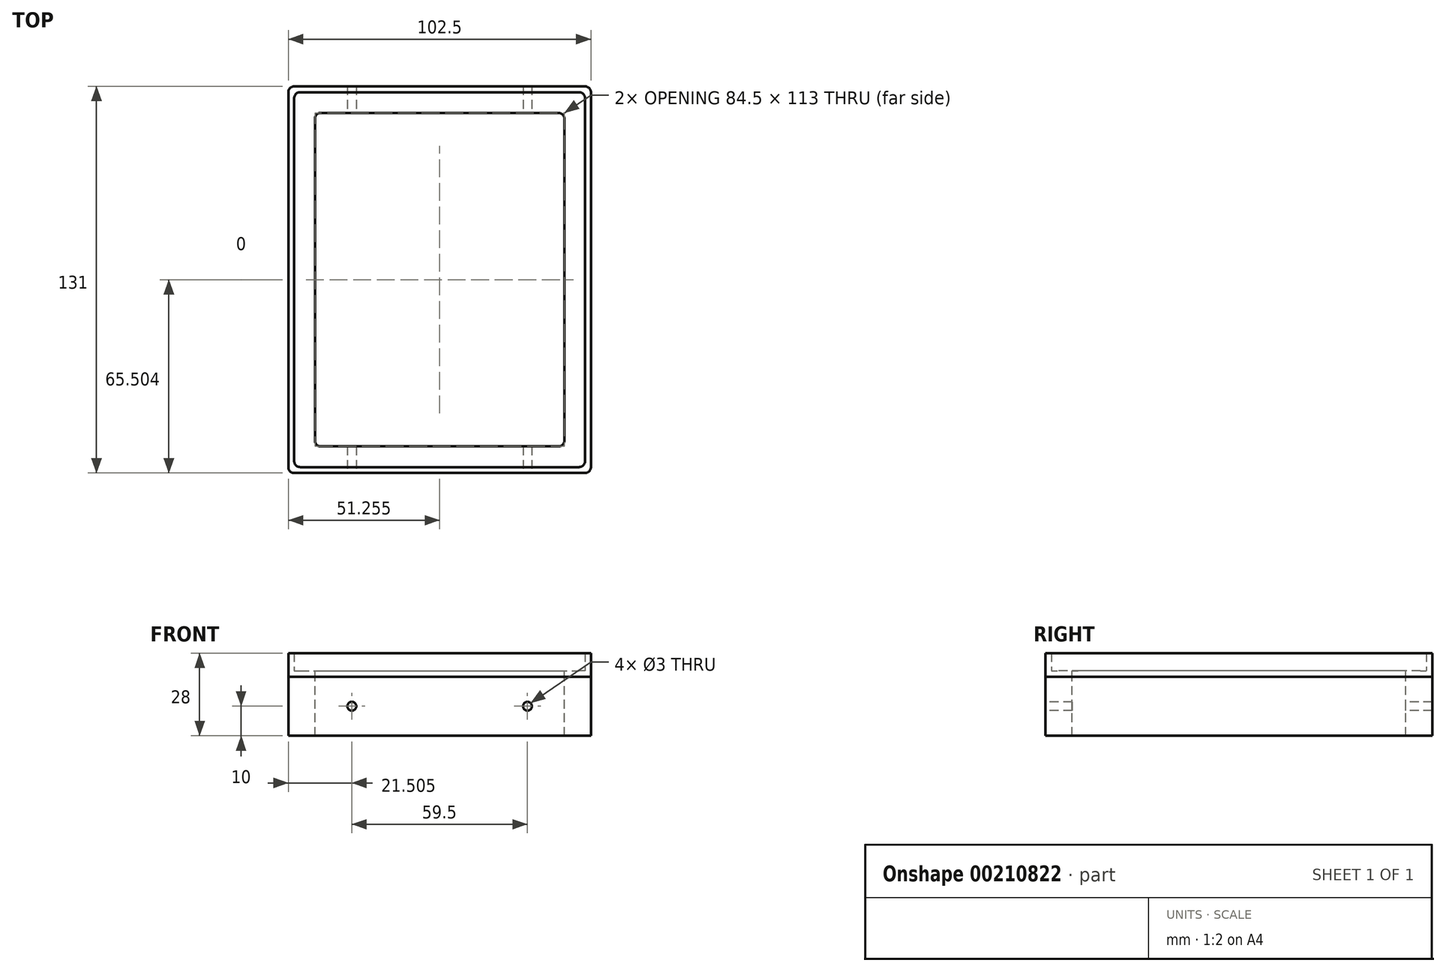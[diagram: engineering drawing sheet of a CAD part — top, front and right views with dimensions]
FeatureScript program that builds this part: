
annotation { "Feature Type Name" : "Feature", "Feature Type Description" : "" }
export const myFeature = defineFeature(function(context is Context, id is Id, definition is map)
    precondition{}
    {
        {
            var Q0;
            Q0=qCreatedBy(makeId("Top.planeOp"),FACE);
            var sketch = newSketch(context, id + "F0", { "sketchPlane" : qUnion([Q0])});
            skLineSegment(sketch, "E0.bottom", {"start": v(-48.46, 61.26) * mm, "end": v(46.04, 61.26) * mm});
            skLineSegment(sketch, "E0.top", {"start": v(-48.46, -65.74) * mm, "end": v(46.04, -65.74) * mm});
            skLineSegment(sketch, "E0.left", {"start": v(-50.46, 59.26) * mm, "end": v(-50.46, -63.74) * mm});
            skLineSegment(sketch, "E0.right", {"start": v(48.04, 59.26) * mm, "end": v(48.04, -63.74) * mm});
            skLineSegment(sketch, "E1.bottom", {"start": v(-50.46, 63.26) * mm, "end": v(48.04, 63.26) * mm});
            skLineSegment(sketch, "E1.top", {"start": v(-50.46, -67.74) * mm, "end": v(48.04, -67.74) * mm});
            skLineSegment(sketch, "E1.left", {"start": v(-52.46, 61.26) * mm, "end": v(-52.46, -65.74) * mm});
            skLineSegment(sketch, "E1.right", {"start": v(50.04, 61.26) * mm, "end": v(50.04, -65.74) * mm});
            skPoint(sketch, "E2.visualSharp", {"position": v(48.04, 61.26) * mm});
            skArc(sketch, "E2.filletArc", {"start": v(48.04, 59.26) * mm, "mid": v(47.46, 60.68) * mm, "end": v(46.04, 61.26) * mm});
            skPoint(sketch, "E3.visualSharp", {"position": v(50.04, 63.26) * mm});
            skArc(sketch, "E3.filletArc", {"start": v(50.04, 61.26) * mm, "mid": v(49.46, 62.68) * mm, "end": v(48.04, 63.26) * mm});
            skPoint(sketch, "E4.visualSharp", {"position": v(-50.46, 61.26) * mm});
            skArc(sketch, "E4.filletArc", {"start": v(-48.46, 61.26) * mm, "mid": v(-49.87, 60.68) * mm, "end": v(-50.46, 59.26) * mm});
            skPoint(sketch, "E5.visualSharp", {"position": v(-52.46, 63.26) * mm});
            skArc(sketch, "E5.filletArc", {"start": v(-50.46, 63.26) * mm, "mid": v(-51.87, 62.68) * mm, "end": v(-52.46, 61.26) * mm});
            skPoint(sketch, "E6.visualSharp", {"position": v(48.04, -65.74) * mm});
            skArc(sketch, "E6.filletArc", {"start": v(46.04, -65.74) * mm, "mid": v(47.46, -65.15) * mm, "end": v(48.04, -63.74) * mm});
            skPoint(sketch, "E7.visualSharp", {"position": v(50.04, -67.74) * mm});
            skArc(sketch, "E7.filletArc", {"start": v(48.04, -67.74) * mm, "mid": v(49.46, -67.15) * mm, "end": v(50.04, -65.74) * mm});
            skPoint(sketch, "E8.visualSharp", {"position": v(-50.46, -65.74) * mm});
            skArc(sketch, "E8.filletArc", {"start": v(-50.46, -63.74) * mm, "mid": v(-49.87, -65.15) * mm, "end": v(-48.46, -65.74) * mm});
            skPoint(sketch, "E9.visualSharp", {"position": v(-52.46, -67.74) * mm});
            skArc(sketch, "E9.filletArc", {"start": v(-52.46, -65.74) * mm, "mid": v(-51.87, -67.15) * mm, "end": v(-50.46, -67.74) * mm});
            skSolve(sketch);
        }
        {
            var Q0;
            Q0=qSketchRegion(id+"F0",true);
            extrude(context, id + "F1", {"entities" : qUnion([Q0]), "depth" : 6 * mm});
        }
        {
            var Q0;
            Q0=qCreatedBy(makeId("Top.planeOp"),FACE);
            var sketch = newSketch(context, id + "F2", { "sketchPlane" : qUnion([Q0])});
            skLineSegment(sketch, "E10.bottom", {"start": v(-50.46, 63.26) * mm, "end": v(48.04, 63.26) * mm});
            skLineSegment(sketch, "E10.top", {"start": v(-50.46, -67.74) * mm, "end": v(48.04, -67.74) * mm});
            skLineSegment(sketch, "E10.left", {"start": v(-52.46, 61.26) * mm, "end": v(-52.46, -65.74) * mm});
            skLineSegment(sketch, "E10.right", {"start": v(50.04, 61.26) * mm, "end": v(50.04, -65.74) * mm});
            skLineSegment(sketch, "E11.bottom", {"start": v(-41.46, 54.26) * mm, "end": v(39.04, 54.26) * mm});
            skLineSegment(sketch, "E11.top", {"start": v(-41.46, -58.74) * mm, "end": v(39.04, -58.74) * mm});
            skLineSegment(sketch, "E11.left", {"start": v(-43.46, 52.26) * mm, "end": v(-43.46, -56.74) * mm});
            skLineSegment(sketch, "E11.right", {"start": v(41.04, 52.26) * mm, "end": v(41.04, -56.74) * mm});
            skPoint(sketch, "E12.visualSharp", {"position": v(-43.46, -58.74) * mm});
            skArc(sketch, "E12.filletArc", {"start": v(-43.46, -56.74) * mm, "mid": v(-42.87, -58.15) * mm, "end": v(-41.46, -58.74) * mm});
            skPoint(sketch, "E13.visualSharp", {"position": v(41.04, -58.74) * mm});
            skArc(sketch, "E13.filletArc", {"start": v(39.04, -58.74) * mm, "mid": v(40.46, -58.15) * mm, "end": v(41.04, -56.74) * mm});
            skPoint(sketch, "E14.visualSharp", {"position": v(41.04, 54.26) * mm});
            skArc(sketch, "E14.filletArc", {"start": v(41.04, 52.26) * mm, "mid": v(40.46, 53.68) * mm, "end": v(39.04, 54.26) * mm});
            skPoint(sketch, "E15.visualSharp", {"position": v(-43.46, 54.26) * mm});
            skArc(sketch, "E15.filletArc", {"start": v(-41.46, 54.26) * mm, "mid": v(-42.87, 53.68) * mm, "end": v(-43.46, 52.26) * mm});
            skPoint(sketch, "E16.visualSharp", {"position": v(-52.46, -67.74) * mm});
            skArc(sketch, "E16.filletArc", {"start": v(-52.46, -65.74) * mm, "mid": v(-51.87, -67.15) * mm, "end": v(-50.46, -67.74) * mm});
            skPoint(sketch, "E17.visualSharp", {"position": v(50.04, -67.74) * mm});
            skArc(sketch, "E17.filletArc", {"start": v(48.04, -67.74) * mm, "mid": v(49.46, -67.15) * mm, "end": v(50.04, -65.74) * mm});
            skPoint(sketch, "E18.visualSharp", {"position": v(50.04, 63.26) * mm});
            skArc(sketch, "E18.filletArc", {"start": v(50.04, 61.26) * mm, "mid": v(49.46, 62.68) * mm, "end": v(48.04, 63.26) * mm});
            skPoint(sketch, "E19.visualSharp", {"position": v(-52.46, 63.26) * mm});
            skArc(sketch, "E19.filletArc", {"start": v(-50.46, 63.26) * mm, "mid": v(-51.87, 62.68) * mm, "end": v(-52.46, 61.26) * mm});
            skSolve(sketch);
        }
        {
            var Q0;
            Q0=qSketchRegion(id+"F2",true);
            extrude(context, id + "F3", {"entities" : qUnion([Q0]), "operationType" : NewBodyOperationType.ADD, "oppositeDirection" : true, "depth" : 2 * mm});
        }
        {
            var Q0;
            Q0=makeQuery(id+"F3.opExtrude","CAP_FACE",FACE,{"disambiguationData":[OSD([sQuery(id+"F2.wireOp",EDGE,"E10.bottom"),sQuery(id+"F2.wireOp",EDGE,"E10.top"),sQuery(id+"F2.wireOp",EDGE,"E10.left"),sQuery(id+"F2.wireOp",EDGE,"E10.right"),sQuery(id+"F2.wireOp",EDGE,"E11.bottom"),sQuery(id+"F2.wireOp",EDGE,"E11.top"),sQuery(id+"F2.wireOp",EDGE,"E11.left"),sQuery(id+"F2.wireOp",EDGE,"E11.right"),sQuery(id+"F2.wireOp",EDGE,"E12.filletArc"),sQuery(id+"F2.wireOp",EDGE,"E13.filletArc"),sQuery(id+"F2.wireOp",EDGE,"E14.filletArc"),sQuery(id+"F2.wireOp",EDGE,"E15.filletArc"),sQuery(id+"F2.wireOp",EDGE,"E16.filletArc"),sQuery(id+"F2.wireOp",EDGE,"E17.filletArc"),sQuery(id+"F2.wireOp",EDGE,"E18.filletArc"),sQuery(id+"F2.wireOp",EDGE,"E19.filletArc")])],"isStart":false});
            extrude(context, id + "F4", {"entities" : qUnion([Q0]), "depth" : 20 * mm});
        }
        {
            var Q0;
            Q0=makeQuery(id+"F4.opExtrude","SWEPT_FACE",FACE,{"disambiguationData":[OSD([sQuery(id+"F2.wireOp",EDGE,"E10.top")])]});
            var sketch = newSketch(context, id + "F5", { "sketchPlane" : qUnion([Q0])});
            skCircle(sketch, "E20", {"center": v(28.54, -12) * mm, "radius": 1.5 * mm});
            skCircle(sketch, "E21", {"center": v(-30.96, -12) * mm, "radius": 1.5 * mm});
            skSolve(sketch);
        }
        {
            var Q0;
            Q0=qSketchRegion(id+"F5",true);
            extrude(context, id + "F6", {"entities" : qUnion([Q0]), "operationType" : NewBodyOperationType.REMOVE, "oppositeDirection" : true, "depth" : 135 * mm});
        }
    });
